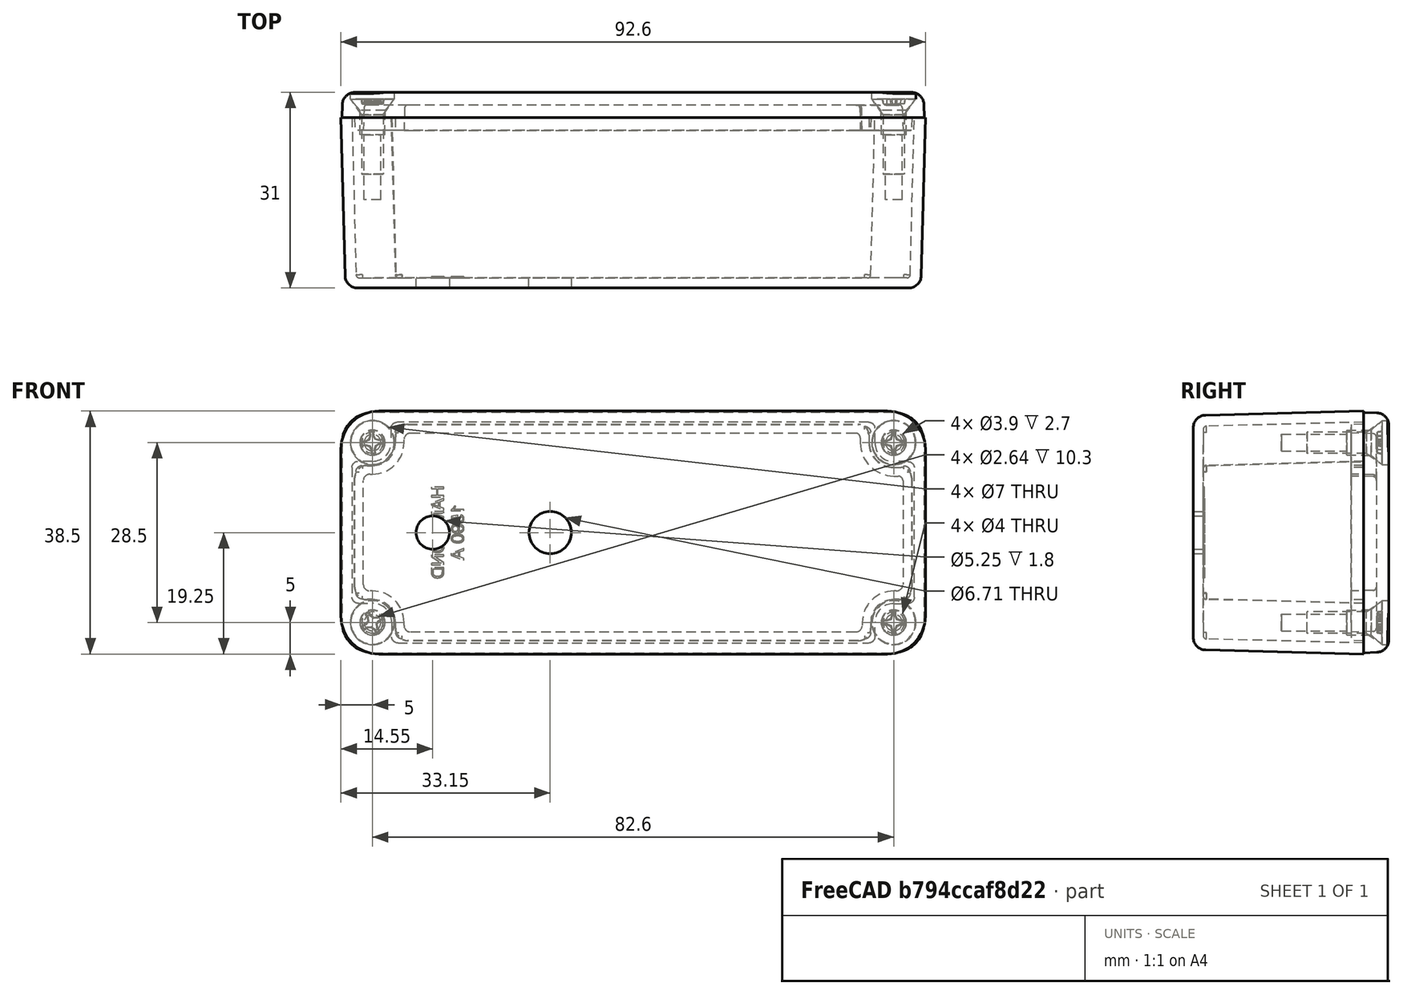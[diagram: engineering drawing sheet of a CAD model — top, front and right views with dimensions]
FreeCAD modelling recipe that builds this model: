
FCSTD DOCUMENT  (FreeCAD 0.19R16830 +1504 (Git))
Label: 1590a-drill-test
License: All rights reserved
LicenseURL: http://en.wikipedia.org/wiki/All_rights_reserved
objects: App::LinkGroup×1, Part::Feature×1, Sketcher::SketchObject×1, PartDesign::FeatureBase×1, PartDesign::Pocket×1, PartDesign::Body×1
note: 6 computed .brp shape members not serialized (recipe doc carries the construction recipe); baked Part::Feature solids carry a one-line shape summary decoded from their .brp

FEATURE [App::LinkGroup] LinkGroup
  LinkMode = 0
FEATURE [Part::Feature] Feature  label="Hammond 1590A"
  shape: bbox 92.97 x 207.7 x 38.77 mm, 452 faces, 6 solids (baked)
FEATURE [Sketcher::SketchObject] Sketch  label="DrillPatternTopSketch"
  MapMode = 5
  Placement = pos=(0,0,0) rot=(1,0,0;1.5708rad)
  Support = -> [XZ_Plane]
  sketch-geometry (2):
    g0: Circle CenterX=-31.75 CenterY=0 CenterZ=0 NormalX=0 NormalY=0 NormalZ=1 AngleXU=0 Radius=2.62566
    g1: Circle CenterX=-13.1495 CenterY=0 CenterZ=0 NormalX=0 NormalY=0 NormalZ=1 AngleXU=0 Radius=3.35489
  constraints (2):
    c: PointOnObject(g0,g-1)
    c: PointOnObject(g1,g-1)
FEATURE [PartDesign::FeatureBase] BaseFeature
  BaseFeature = -> Feature
FEATURE [PartDesign::Pocket] Pocket  label="DrillPatternTopPocket"
  BaseFeature = -> BaseFeature
  ClaimChildren = false
  Length = 0
  Length2 = 100
  Profile = -> Sketch
  Reversed = true
  Type = 1
FEATURE [PartDesign::Body] Body
  BaseFeature = -> Feature
  Group = -> [BaseFeature,Sketch,Pocket]
  Origin = -> Origin
  Tip = -> Pocket
